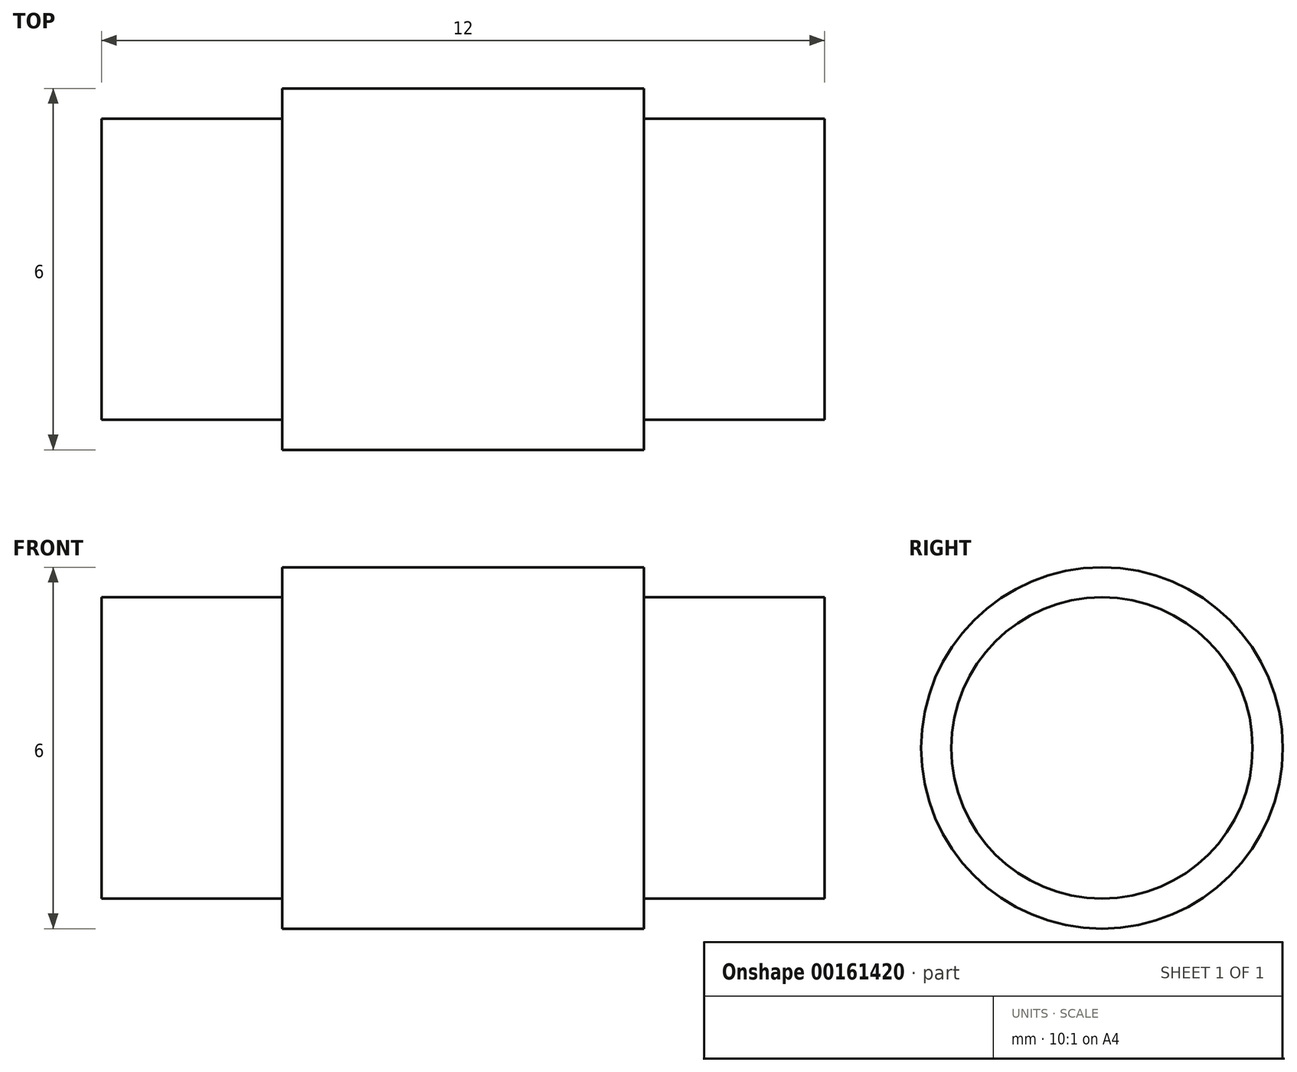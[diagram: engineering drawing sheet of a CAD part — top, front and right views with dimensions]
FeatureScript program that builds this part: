
annotation { "Feature Type Name" : "Feature", "Feature Type Description" : "" }
export const myFeature = defineFeature(function(context is Context, id is Id, definition is map)
    precondition{}
    {
        {
            var Q0;
            Q0=qCreatedBy(makeId("Right.planeOp"),FACE);
            var sketch = newSketch(context, id + "F0", { "sketchPlane" : qUnion([Q0])});
            skCircle(sketch, "E0", {"center": v(0, 0) * mm, "radius": 2.5 * mm});
            skSolve(sketch);
        }
        {
            var Q0;
            Q0=qSketchRegion(id+"F0",true);
            extrude(context, id + "F1", {"entities" : qUnion([Q0]), "depth" : 3 * mm});
        }
        {
            var Q0;
            Q0=makeQuery(id+"F1.opExtrude","CAP_FACE",FACE,{"disambiguationData":[OSD([sQuery(id+"F0.wireOp",EDGE,"E0")])],"isStart":false});
            var sketch = newSketch(context, id + "F2", { "sketchPlane" : qUnion([Q0])});
            skCircle(sketch, "E1", {"center": v(0, 0) * mm, "radius": 3 * mm});
            skSolve(sketch);
        }
        {
            var Q0;
            Q0 = qSketchRegion(id + "F2", true);
            extrude(context, id + "F3", {"entities" : qUnion([Q0]), "operationType" : NewBodyOperationType.ADD, "depth" : 6 * mm});
        }
        {
            var Q0;
            Q0=makeQuery(id+"F3.opExtrude","CAP_FACE",FACE,{"disambiguationData":[OSD([sQuery(id+"F2.wireOp",EDGE,"E1")])],"isStart":false});
            var sketch = newSketch(context, id + "F4", { "sketchPlane" : qUnion([Q0])});
            skCircle(sketch, "E2", {"center": v(0, 0) * mm, "radius": 2.5 * mm});
            skSolve(sketch);
        }
        {
            var Q0;
            Q0 = qSketchRegion(id + "F4", true);
            extrude(context, id + "F5", {"entities" : qUnion([Q0]), "operationType" : NewBodyOperationType.ADD, "depth" : 3 * mm});
        }
    });
